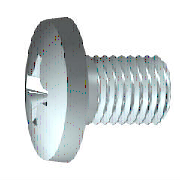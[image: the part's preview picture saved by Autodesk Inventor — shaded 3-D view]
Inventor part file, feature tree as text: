
AUTODESK INVENTOR PART (.ipt)
format: ipt  version: 2013 (Build 170138000, 138)  size: 247,808 bytes
history: native  units: mm (DEFAULTED — no unit token found)
features: other x2, extrude x1, plane x1
ambient origin geometry x7: Origin, YZ Plane, XZ Plane, X Axis, Y Axis, Z Axis, Center Point
bodies: Solid1 (feature_tree), Body (feature_tree)
feature tree (4):
  other  "IDS_WORKPLANE{1}"
  extrude  "Slot"  Depth=1.524mm
  other  "Cut"
  plane  "Work Plane3"
